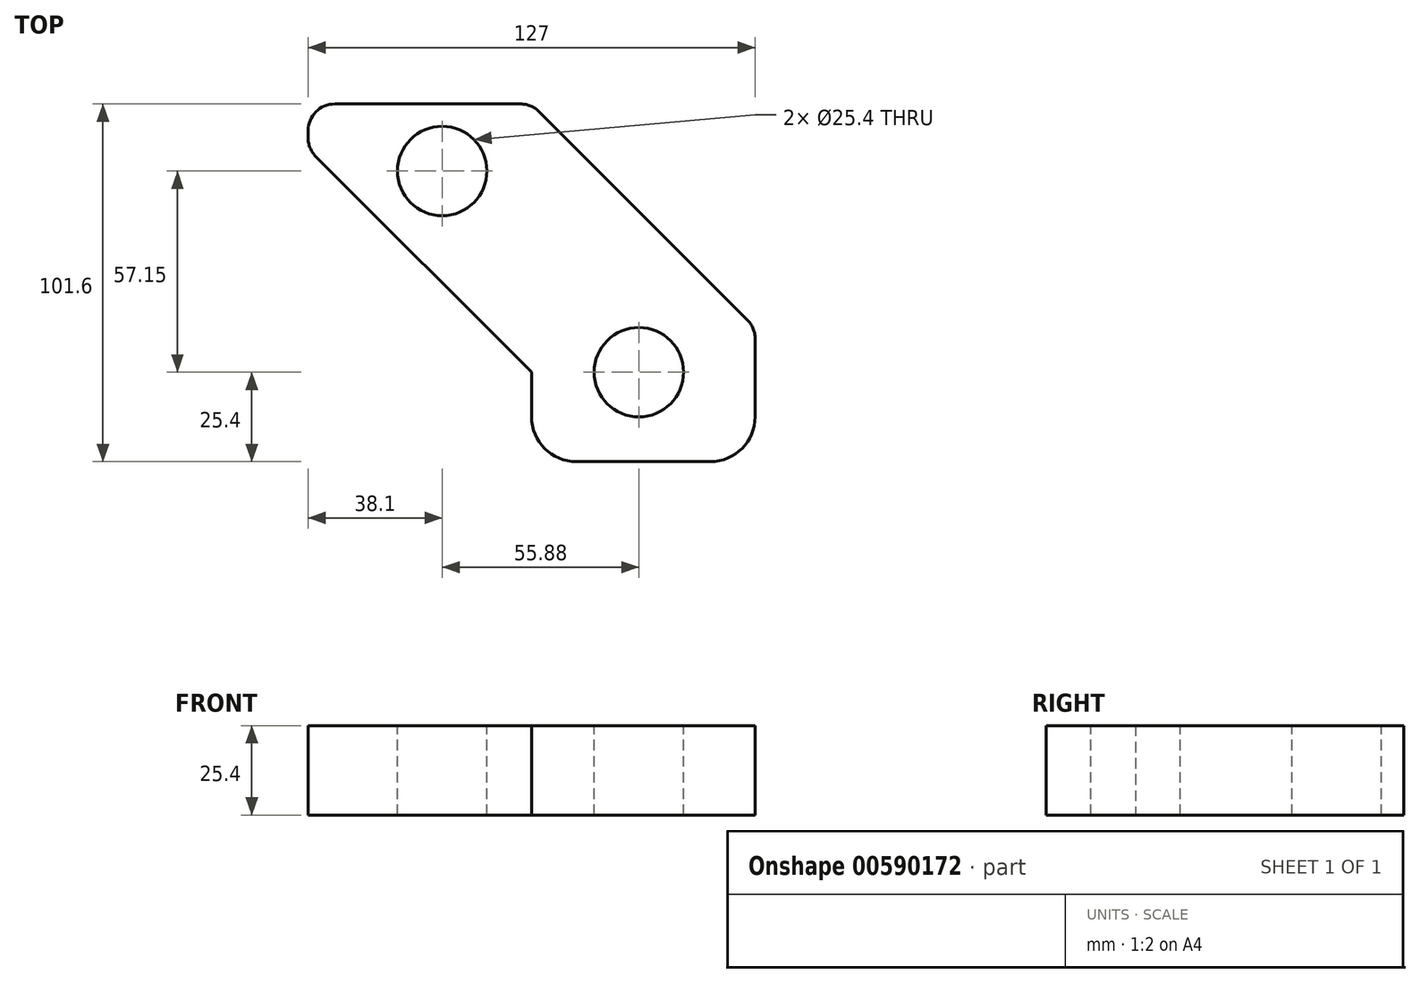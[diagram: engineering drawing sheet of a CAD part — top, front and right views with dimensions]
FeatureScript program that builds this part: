
annotation { "Feature Type Name" : "Feature", "Feature Type Description" : "" }
export const myFeature = defineFeature(function(context is Context, id is Id, definition is map)
    precondition{}
    {
        {
            var Q0;
            Q0=qCreatedBy(makeId("Top.planeOp"),FACE);
            var sketch = newSketch(context, id + "F0", { "sketchPlane" : qUnion([Q0])});
            skLineSegment(sketch, "E0.bottom", {"start": v(63.5, -38.1) * mm, "end": v(-63.5, -38.1) * mm});
            skLineSegment(sketch, "E0.top", {"start": v(63.5, 38.1) * mm, "end": v(-63.5, 38.1) * mm});
            skLineSegment(sketch, "E0.left", {"start": v(63.5, -38.1) * mm, "end": v(63.5, 38.1) * mm});
            skLineSegment(sketch, "E0.right", {"start": v(-63.5, -38.1) * mm, "end": v(-63.5, 38.1) * mm});
            skPoint(sketch, "E0.middle", {"position": v(0, 0) * mm});
            skSolve(sketch);
        }
        {
            var Q0;
            Q0=makeQuery(id+"F0.imprint","IMPRINT",FACE,{"disambiguationData":[TD([[makeQuery(id+"F0.imprint","IMPRINT",EDGE,{"derivedFrom":sQuery(id+"F0.wireOp",EDGE,"E0.bottom")}),-1.0]])]});
            extrude(context, id + "F1", {"entities" : qUnion([Q0]), "depth" : 25.4 * mm, "offsetDistance" : 25.4 * mm});
        }
        {
            var Q0;
            Q0=makeQuery(id+"F1.opExtrude","SWEPT_EDGE",EDGE,{"disambiguationData":[OSD([sQuery(id+"F0.wireOp",EDGE,"E0.bottom"),sQuery(id+"F0.wireOp",EDGE,"E0.right")])]});
            chamfer(context, id + "F2", {"entities" : qUnion([Q0]), "width" : 63.5 * mm, "tangentPropagation" : true});
        }
        {
            var Q0;
            Q0=makeQuery(id+"F1.opExtrude","SWEPT_FACE",FACE,{"disambiguationData":[OSD([sQuery(id+"F0.wireOp",EDGE,"E0.bottom")])]});
            var sketch = newSketch(context, id + "F3", { "sketchPlane" : qUnion([Q0])});
            skLineSegment(sketch, "E1.bottom", {"start": v(0, 0) * mm, "end": v(63.5, 0) * mm});
            skLineSegment(sketch, "E1.top", {"start": v(0, 25.4) * mm, "end": v(63.5, 25.4) * mm});
            skLineSegment(sketch, "E1.left", {"start": v(0, 0) * mm, "end": v(0, 25.4) * mm});
            skLineSegment(sketch, "E1.right", {"start": v(63.5, 0) * mm, "end": v(63.5, 25.4) * mm});
            skSolve(sketch);
        }
        {
            var Q0;
            Q0=makeQuery(id+"F3.imprint","IMPRINT",FACE,{"disambiguationData":[TD([[makeQuery(id+"F3.imprint","IMPRINT",EDGE,{"derivedFrom":sQuery(id+"F3.wireOp",EDGE,"E1.bottom")}),-1.0]])]});
            extrude(context, id + "F4", {"entities" : qUnion([Q0]), "operationType" : NewBodyOperationType.ADD, "depth" : 25.4 * mm, "offsetDistance" : 25.4 * mm});
        }
        {
            var Q0;
            Q0=makeQuery(id+"F1.opExtrude","SWEPT_EDGE",EDGE,{"disambiguationData":[OSD([sQuery(id+"F0.wireOp",EDGE,"E0.top"),sQuery(id+"F0.wireOp",EDGE,"E0.left")])]});
            chamfer(context, id + "F5", {"entities" : qUnion([Q0]), "width" : 63.5 * mm, "tangentPropagation" : true});
        }
        {
            var Q0;
            Q0=makeQuery(id+"F4.opExtrude","CAP_EDGE",EDGE,{"disambiguationData":[OSD([sQuery(id+"F3.wireOp",EDGE,"E1.right")])],"isStart":false});
            var Q1;
            Q1=makeQuery(id+"F4.opExtrude","CAP_EDGE",EDGE,{"disambiguationData":[OSD([sQuery(id+"F3.wireOp",EDGE,"E1.left")])],"isStart":false});
            fillet(context, id + "F6", {"entities" : qUnion([Q0, Q1]), "radius" : 12.7 * mm, "tangentPropagation" : true, "allowEdgeOverflow" : false});
        }
        {
            var Q0;
            {var subQ0=sQuery(id+"F0.wireOp",EDGE,"E0.right");Q0=makeQuery(id+"F2.opChamfer","BLEND_EDGE",EDGE,{"blendedFrom":[makeQuery(id+"F1.opExtrude","SWEPT_EDGE",EDGE,{"disambiguationData":[OSD([sQuery(id+"F0.wireOp",EDGE,"E0.bottom"),subQ0])]}),makeQuery(id+"F1.opExtrude","SWEPT_FACE",FACE,{"disambiguationData":[OSD([subQ0])]})],"blendedInto":[makeQuery(id+"F1.opExtrude","SWEPT_FACE",FACE,{"disambiguationData":[OSD([subQ0])]})]});}
            var Q1;
            Q1=makeQuery(id+"F1.opExtrude","SWEPT_EDGE",EDGE,{"disambiguationData":[OSD([sQuery(id+"F0.wireOp",EDGE,"E0.top"),sQuery(id+"F0.wireOp",EDGE,"E0.right")])]});
            var Q2;
            {var subQ0=sQuery(id+"F0.wireOp",EDGE,"E0.top");Q2=makeQuery(id+"F5.opChamfer","BLEND_EDGE",EDGE,{"blendedFrom":[makeQuery(id+"F1.opExtrude","SWEPT_EDGE",EDGE,{"disambiguationData":[OSD([subQ0,sQuery(id+"F0.wireOp",EDGE,"E0.left")])]}),makeQuery(id+"F1.opExtrude","SWEPT_FACE",FACE,{"disambiguationData":[OSD([subQ0])]})],"blendedInto":[makeQuery(id+"F1.opExtrude","SWEPT_FACE",FACE,{"disambiguationData":[OSD([subQ0])]})]});}
            var Q3;
            {var subQ0=sQuery(id+"F0.wireOp",EDGE,"E0.left");Q3=makeQuery(id+"F5.opChamfer","BLEND_EDGE",EDGE,{"blendedFrom":[makeQuery(id+"F1.opExtrude","SWEPT_EDGE",EDGE,{"disambiguationData":[OSD([sQuery(id+"F0.wireOp",EDGE,"E0.top"),subQ0])]}),makeQuery(id+"F4.boolean.opBoolean","MERGE",FACE,{"derivedFrom":[makeQuery(id+"F1.opExtrude","SWEPT_FACE",FACE,{"disambiguationData":[OSD([subQ0])]}),makeQuery(id+"F4.opExtrude","SWEPT_FACE",FACE,{"disambiguationData":[OSD([sQuery(id+"F3.wireOp",EDGE,"E1.right")])]})]})],"blendedInto":[makeQuery(id+"F4.boolean.opBoolean","MERGE",FACE,{"derivedFrom":[makeQuery(id+"F1.opExtrude","SWEPT_FACE",FACE,{"disambiguationData":[OSD([subQ0])]}),makeQuery(id+"F4.opExtrude","SWEPT_FACE",FACE,{"disambiguationData":[OSD([sQuery(id+"F3.wireOp",EDGE,"E1.right")])]})]})]});}
            fillet(context, id + "F7", {"entities" : qUnion([Q0, Q1, Q2, Q3]), "radius" : 7.62 * mm, "tangentPropagation" : true, "allowEdgeOverflow" : false});
        }
        {
            var Q0;
            Q0=makeQuery(id+"F4.boolean.opBoolean","MERGE",FACE,{"derivedFrom":[makeQuery(id+"F1.opExtrude","CAP_FACE",FACE,{"disambiguationData":[OSD([sQuery(id+"F0.wireOp",EDGE,"E0.bottom"),sQuery(id+"F0.wireOp",EDGE,"E0.top"),sQuery(id+"F0.wireOp",EDGE,"E0.left"),sQuery(id+"F0.wireOp",EDGE,"E0.right")])],"isStart":false}),makeQuery(id+"F4.opExtrude","SWEPT_FACE",FACE,{"disambiguationData":[OSD([sQuery(id+"F3.wireOp",EDGE,"E1.top")])]})]});
            var sketch = newSketch(context, id + "F8", { "sketchPlane" : qUnion([Q0])});
            skPoint(sketch, "E2", {"position": v(30.48, -38.1) * mm});
            skSolve(sketch);
        }
        {
            var Q0;
            Q0=sQuery(id+"F8.wireOp",VERTEX,"E2");
            var Q1;
            Q1=makeQuery(id+"F1.opExtrude","SWEPT_BODY",BODY,{"disambiguationData":[OSD([sQuery(id+"F0.wireOp",EDGE,"E0.bottom"),sQuery(id+"F0.wireOp",EDGE,"E0.top"),sQuery(id+"F0.wireOp",EDGE,"E0.left"),sQuery(id+"F0.wireOp",EDGE,"E0.right")])]});
            hole(context, id + "F9", {"style" : HoleStyle.SIMPLE, "endStyle" : HoleEndStyle.THROUGH, "holeDiameter" : 25.4 * mm, "majorDiameter" : 6.35 * mm, "isTappedThrough" : true, "tappedDepth" : 12.7 * mm, "tapClearance" : 3, "locations" : qUnion([Q0]), "scope" : qUnion([Q1])});
        }
        {
            var Q0;
            Q0=makeQuery(id+"F4.boolean.opBoolean","MERGE",FACE,{"derivedFrom":[makeQuery(id+"F1.opExtrude","CAP_FACE",FACE,{"disambiguationData":[OSD([sQuery(id+"F0.wireOp",EDGE,"E0.bottom"),sQuery(id+"F0.wireOp",EDGE,"E0.top"),sQuery(id+"F0.wireOp",EDGE,"E0.left"),sQuery(id+"F0.wireOp",EDGE,"E0.right")])],"isStart":false}),makeQuery(id+"F4.opExtrude","SWEPT_FACE",FACE,{"disambiguationData":[OSD([sQuery(id+"F3.wireOp",EDGE,"E1.top")])]})]});
            var sketch = newSketch(context, id + "F10", { "sketchPlane" : qUnion([Q0])});
            skPoint(sketch, "E3", {"position": v(-25.4, 19.05) * mm});
            skSolve(sketch);
        }
        {
            var Q0;
            Q0=sQuery(id+"F10.wireOp",VERTEX,"E3");
            var Q1;
            Q1=makeQuery(id+"F1.opExtrude","SWEPT_BODY",BODY,{"disambiguationData":[OSD([sQuery(id+"F0.wireOp",EDGE,"E0.bottom"),sQuery(id+"F0.wireOp",EDGE,"E0.top"),sQuery(id+"F0.wireOp",EDGE,"E0.left"),sQuery(id+"F0.wireOp",EDGE,"E0.right")])]});
            hole(context, id + "F11", {"style" : HoleStyle.SIMPLE, "endStyle" : HoleEndStyle.THROUGH, "holeDiameter" : 25.4 * mm, "majorDiameter" : 6.35 * mm, "isTappedThrough" : true, "tappedDepth" : 12.7 * mm, "tapClearance" : 3, "locations" : qUnion([Q0]), "scope" : qUnion([Q1])});
        }
    });
